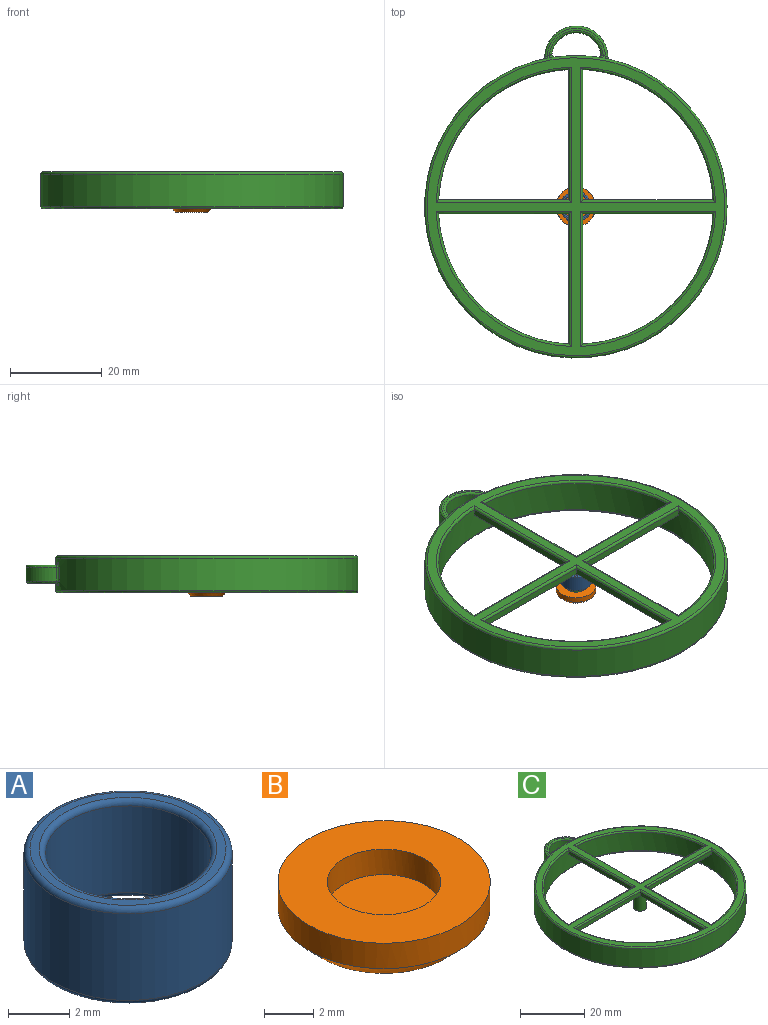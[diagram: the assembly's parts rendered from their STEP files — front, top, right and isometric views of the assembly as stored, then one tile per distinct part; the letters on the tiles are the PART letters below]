
ASSEMBLY  parts=3 mates=2
PART A: 8 faces, bbox 7.4x7.4x3.9 mm
  f0: cylinder r=2.7mm len=5.4mm, axis (0,0,1), area 58.7mm2, adj f4,f6
  f1: cylinder r=3.4mm len=6.8mm, axis (0,0,1), area 73.9mm2, adj f5,f7
  f2: plane 6.4x6.4mm, normal (0,0,-1), area 5.7mm2, adj f6,f7
  f3: plane 6.4x6.4mm, normal (0,0,1), area 5.7mm2, adj f4,f5
  f4: torus R=2.9mm, axis (0,0,1), area 5.5mm2, adj f0,f3
  f5: torus R=3.2mm, axis (0,0,1), area 6.6mm2, adj f1,f3
  f6: torus R=2.9mm, axis (0,0,1), area 5.5mm2, adj f0,f2
  f7: torus R=3.2mm, axis (0,0,1), area 6.6mm2, adj f1,f2
PART B: 6 faces, bbox 8.6x8.6x2.1 mm
  f0: cylinder r=2.3mm len=4.6mm, axis (0,0,-1), area 18.3mm2, adj f2,f5
  f1: cylinder r=4.3mm len=8.6mm, axis (0,0,-1), area 34.2mm2, adj f2,f3
  f2: plane 8.6x8.6mm, normal (0,0,1), area 41.5mm2, adj f0,f1
  f3: cone r=3.5mm half-angle=45deg, axis (0,0,1), area 27.4mm2, adj f1,f4
  f4: plane 7x7mm, normal (0,0,-1), area 38.5mm2, adj f3
  f5: plane 4.6x4.6mm, normal (0,0,1), area 16.6mm2, adj f0
PART C: 54 faces, bbox 71.4x75.7x8 mm
  f0: cylinder r=33mm len=66mm, axis (0,0,-1), area 1427.8mm2, adj f17,f18,f19,f21,f22,f23,f25,f26
  f1: cylinder r=30mm len=60mm, axis (0,0,-1), area 1301.5mm2, adj f8,f9,f10,f11,f12,f13,f14,f15
  f2: plane 65x65mm, normal (0,0,1), area 635.8mm2, adj f37,f38,f39,f40,f41,f42,f43,f44
  f3: plane 65x65mm, normal (0,0,-1), area 395.8mm2, adj f49,f50
  f4: cylinder r=5.39mm len=10.7mm, axis (0,0,-1), area 46.9mm2, adj f17,f20,f24,f25
  f5: cylinder r=6.89mm len=13.78mm, axis (0,0,-1), area 64.3mm2, adj f22,f31,f32,f36
  f6: plane 12.76x6.08mm, normal (0,0,1), area 9.3mm2, adj f20,f21,f30,f31
  f7: plane 12.76x6.08mm, normal (0,0,-1), area 9.3mm2, adj f23,f24,f32,f33
  f8: plane 28.46x1.5mm, normal (1,0,0), area 42.7mm2, adj f1,f15,f16,f46
  f9: plane 28.46x1.5mm, normal (-1,0,0), area 42.7mm2, adj f1,f10,f16,f43
  f10: plane 28.46x1.5mm, normal (0,1,0), area 42.7mm2, adj f1,f9,f16,f44
  f11: plane 28.46x1.5mm, normal (0,-1,0), area 42.7mm2, adj f1,f12,f16,f40
  f12: plane 28.46x1.5mm, normal (-1,0,0), area 42.7mm2, adj f1,f11,f16,f41
  f13: plane 28.46x1.5mm, normal (1,0,0), area 42.7mm2, adj f1,f14,f16,f37
  f14: plane 28.46x1.5mm, normal (0,-1,0), area 42.7mm2, adj f1,f13,f16,f38
  f15: plane 28.46x1.5mm, normal (0,1,0), area 42.7mm2, adj f1,f8,f16,f48
  f16: plane 60x60mm, normal (0,0,-1), area 338.3mm2, adj f1,f8,f9,f10,f11,f12,f13,f14
  f17: cylinder r=0.5mm len=3mm, axis (0,0,-1), area 2.8mm2, adj f0,f4,f18,f19
  f18: bspline ~1.22x1.17mm, area 0.9mm2, adj f0,f17,f20,f21
  f19: bspline ~1.24x1.2mm, area 0.9mm2, adj f0,f17,f23,f24
  f20: torus R=5.89mm, axis (0,0,1), area 12.9mm2, adj f4,f6,f18,f26
  f21: torus R=33.5mm, axis (0,0,1), area 0.4mm2, adj f0,f6,f18,f27
  f22: cylinder r=0.5mm len=3mm, axis (0,0,1), area 2mm2, adj f0,f5,f27,f28
  f23: torus R=33.5mm, axis (0,0,1), area 0.4mm2, adj f0,f7,f19,f28
  f24: torus R=5.89mm, axis (0,0,1), area 12.9mm2, adj f4,f7,f19,f29
  f25: cylinder r=0.5mm len=3mm, axis (0,0,-1), area 2.8mm2, adj f0,f4,f26,f29
  f26: bspline ~1.24x1.2mm, area 0.9mm2, adj f0,f20,f25,f30
  f27: bspline ~1.22x1.19mm, area 0.8mm2, adj f0,f21,f22,f31
  f28: bspline ~1.22x1.14mm, area 0.8mm2, adj f0,f22,f23,f32
  f29: bspline ~1.22x1.17mm, area 0.9mm2, adj f0,f24,f25,f33
  f30: torus R=33.5mm, axis (0,0,1), area 0.4mm2, adj f0,f6,f26,f34
  f31: torus R=6.39mm, axis (0,0,1), area 16.3mm2, adj f5,f6,f27,f34
  f32: torus R=6.39mm, axis (0,0,1), area 16.3mm2, adj f5,f7,f28,f35
  f33: torus R=33.5mm, axis (0,0,1), area 0.4mm2, adj f0,f7,f29,f35
  f34: bspline ~1.22x1.14mm, area 0.8mm2, adj f0,f30,f31,f36
  f35: bspline ~1.22x1.19mm, area 0.8mm2, adj f0,f32,f33,f36
  f36: cylinder r=0.5mm len=3mm, axis (0,0,1), area 2mm2, adj f0,f5,f34,f35
  f37: cylinder r=0.5mm len=29.48mm, axis (0,1,0), area 22.6mm2, adj f2,f13,f38,f39
  f38: cylinder r=0.5mm len=29.48mm, axis (1,0,0), area 22.6mm2, adj f2,f14,f37,f39
  f39: torus R=30.5mm, axis (0,0,1), area 35.2mm2, adj f1,f2,f37,f38
  f40: cylinder r=0.5mm len=29.48mm, axis (1,0,0), area 22.6mm2, adj f2,f11,f41,f42
  f41: cylinder r=0.5mm len=29.48mm, axis (0,-1,0), area 22.6mm2, adj f2,f12,f40,f42
  f42: torus R=30.5mm, axis (0,0,1), area 35.2mm2, adj f1,f2,f40,f41
  f43: cylinder r=0.5mm len=29.48mm, axis (0,-1,0), area 22.6mm2, adj f2,f9,f44,f45
  f44: cylinder r=0.5mm len=29.48mm, axis (-1,0,0), area 22.6mm2, adj f2,f10,f43,f45
  f45: torus R=30.5mm, axis (0,0,1), area 35.2mm2, adj f1,f2,f43,f44
  f46: cylinder r=0.5mm len=29.48mm, axis (0,1,0), area 22.6mm2, adj f2,f8,f47,f48
  f47: torus R=30.5mm, axis (0,0,1), area 35.2mm2, adj f1,f2,f46,f48
  f48: cylinder r=0.5mm len=29.48mm, axis (-1,0,0), area 22.6mm2, adj f2,f15,f46,f47
  f49: torus R=30.5mm, axis (0,0,1), area 148.9mm2, adj f1,f3
  f50: torus R=32.5mm, axis (0,0,1), area 162mm2, adj f0,f3
  f51: torus R=32.5mm, axis (0,0,1), area 162mm2, adj f0,f2
  f52: plane 4x4mm, normal (0,0,-1), area 12.6mm2, adj f53
  f53: cylinder r=2mm len=6mm, axis (0,0,1), area 75.4mm2, adj f16,f52
PLACE A rot(axis=(0,0,-1),85.9deg) t=(0,0,0.2)mm
PLACE B at identity
PLACE C at identity fixed
MATE revolute C.f0 <-> A.f0  axis (0,0,1) through (0,0,2)mm
MATE fastened C.f0 <-> B.f0  axis (0,0,-1) through (0,0,-4)mm
